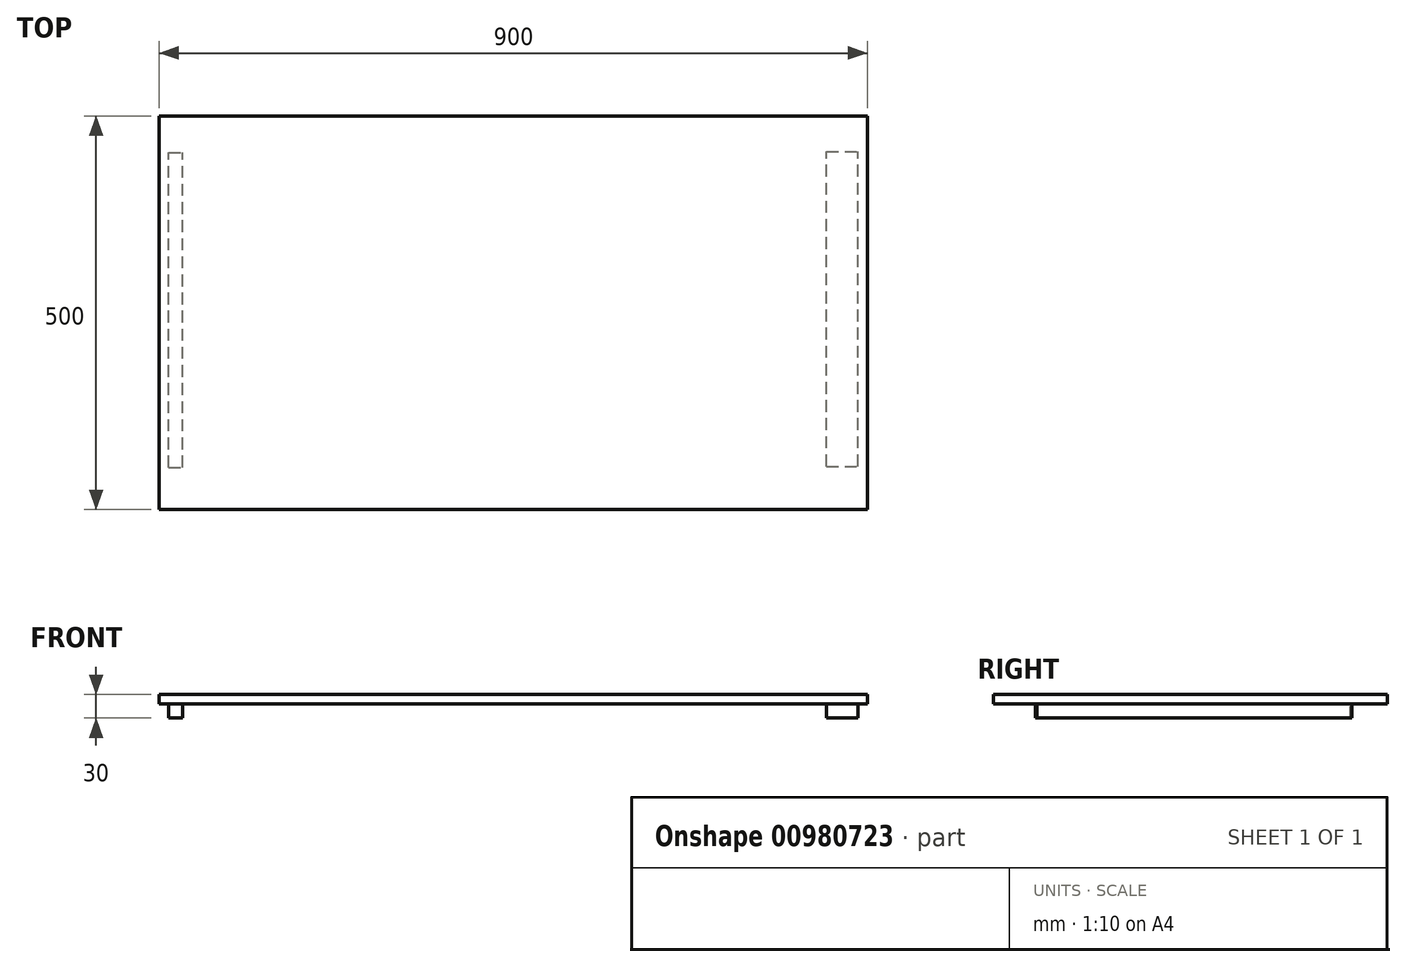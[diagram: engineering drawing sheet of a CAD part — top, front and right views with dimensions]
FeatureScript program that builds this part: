
annotation { "Feature Type Name" : "Feature", "Feature Type Description" : "" }
export const myFeature = defineFeature(function(context is Context, id is Id, definition is map)
    precondition{}
    {
        {
            var Q0;
            Q0=qCreatedBy(makeId("Top.planeOp"),FACE);
            var sketch = newSketch(context, id + "F0", { "sketchPlane" : qUnion([Q0])});
            skLineSegment(sketch, "E0.bottom", {"start": v(-445.7, -423.72) * mm, "end": v(454.3, -423.72) * mm});
            skLineSegment(sketch, "E0.top", {"start": v(-445.7, 76.28) * mm, "end": v(454.3, 76.28) * mm});
            skLineSegment(sketch, "E0.left", {"start": v(-445.7, -423.72) * mm, "end": v(-445.7, 76.28) * mm});
            skLineSegment(sketch, "E0.right", {"start": v(454.3, -423.72) * mm, "end": v(454.3, 76.28) * mm});
            skSolve(sketch);
        }
        {
            var Q0;
            Q0 = qSketchRegion(id + "F0", true);
            extrude(context, id + "F1", {"entities" : qUnion([Q0]), "depth" : 12 * mm, "offsetDistance" : 25.4 * mm});
        }
        {
            var Q0;
            Q0=makeQuery(id+"F1.opExtrude","CAP_FACE",FACE,{"disambiguationData":[OSD([sQuery(id+"F0.wireOp",EDGE,"E0.bottom"),sQuery(id+"F0.wireOp",EDGE,"E0.top"),sQuery(id+"F0.wireOp",EDGE,"E0.left"),sQuery(id+"F0.wireOp",EDGE,"E0.right")])],"isStart":true});
            var sketch = newSketch(context, id + "F2", { "sketchPlane" : qUnion([Q0])});
            skLineSegment(sketch, "E1.bottom", {"start": v(-433.7, 370.3) * mm, "end": v(-415.7, 370.3) * mm});
            skLineSegment(sketch, "E1.top", {"start": v(-433.7, -29.7) * mm, "end": v(-415.7, -29.7) * mm});
            skLineSegment(sketch, "E1.left", {"start": v(-433.7, 370.3) * mm, "end": v(-433.7, -29.7) * mm});
            skLineSegment(sketch, "E1.right", {"start": v(-415.7, 370.3) * mm, "end": v(-415.7, -29.7) * mm});
            skLineSegment(sketch, "E2.bottom", {"start": v(402.3, 368.86) * mm, "end": v(442.3, 368.86) * mm});
            skLineSegment(sketch, "E2.top", {"start": v(402.3, -31.14) * mm, "end": v(442.3, -31.14) * mm});
            skLineSegment(sketch, "E2.left", {"start": v(402.3, 368.86) * mm, "end": v(402.3, -31.14) * mm});
            skLineSegment(sketch, "E2.right", {"start": v(442.3, 368.86) * mm, "end": v(442.3, -31.14) * mm});
            skSolve(sketch);
        }
        {
            var Q0;
            Q0 = qSketchRegion(id + "F2", true);
            extrude(context, id + "F3", {"entities" : qUnion([Q0]), "depth" : 18 * mm, "offsetDistance" : 25.4 * mm});
        }
    });
